# Revit family: Zumtobel MIRO
name_source: partatom
category: Lighting Fixtures
revit_build: Autodesk Revit 2016 (Build: 20150220_1215(x64)
units: mm (PartAtom-declared; Revit-internal decimal feet)

## family parameters
Cut with Voids When Loaded = No
Host = Face
Light Source = Yes
OmniClass Number = 23.80.70.11
OmniClass Title = Luminaries for Internal Lighting
Part Type = Normal
Room Calculation Point = No
Round Connector Dimension = Use Diameter
Shared = No

## types (2) — shared parameters
Apparent Load = 28 VA
Assembly Code = D5020200
Body = Zumtobel_Metal_White
Color Filter = 16777215
Description = Ceiling-recessed LED luminaire - levelling-in
Dimming Lamp Color Temperature Shift = <None>
Emit Shape Visible in Rendering = Yes
Exterior Cover = Zumtobel_MIREL_Lamp_Self_llumination
Height = 85 mm  [stored 0.278871 ft]
Interior Cover = Zumtobel_MIREL_Lamp_Self_llumination_Opaque
Lamp = LED
Manufacturer = Zumtobel Lighting
Tilt Angle = 90.00°
URL = http://www.zumtobel.com
Voltage = 230 V
zero-valued in all types: Default Elevation

## per-type parameters (varying)
| type | Emit from Rectangle Length | Emit from Rectangle Width | Length | Model | Photometric Web File | Width |
| MIRO NIV M625L | 286 mm  [stored 0.93832 ft] | 1224 mm  [stored 4.01575 ft] | 1248 mm  [stored 4.09449 ft] | 42182369 | D33416AA_MIRO_NIV_LED3800-840_M625L_EVG.IES | 310 mm  [stored 1.01706 ft] |
| MIRO M625L | 274 mm  [stored 0.89895 ft] | 1174 mm  [stored 3.85171 ft] | 1198 mm  [stored 3.93045 ft] | 42182371 | 42182371_(STD_LEO).IES | 298 mm  [stored 0.97769 ft] |

note: [stored X ft] marks values corroborated as IEEE doubles in the binary element streams (Revit-internal decimal feet)

## geometry (parser evidence)
native form markers: Blend x8, Sweep x2
no freeform markers — native parametric forms only
